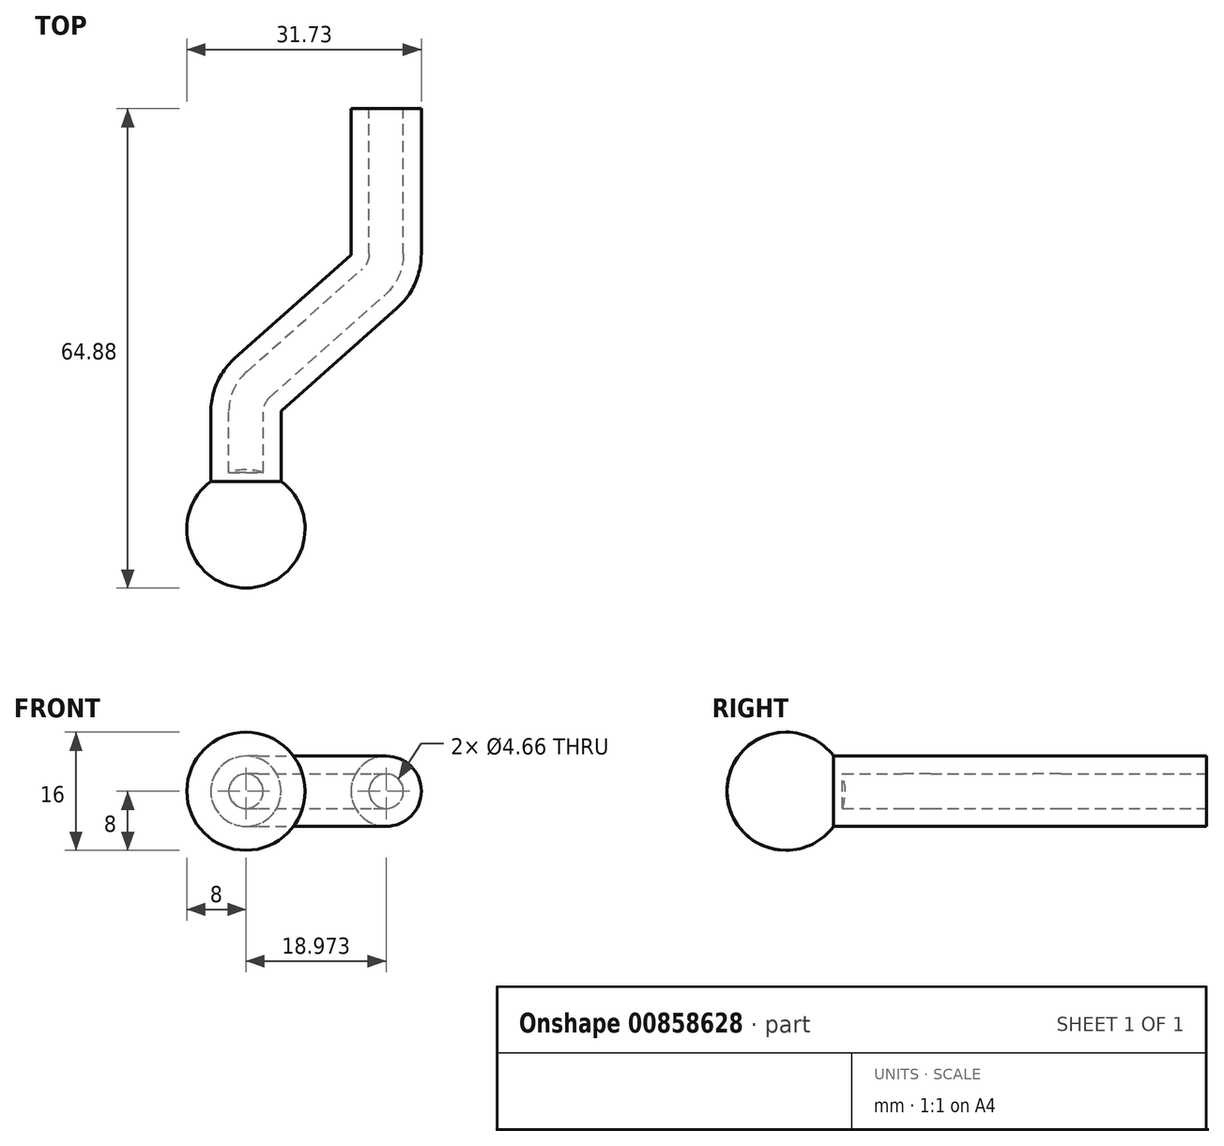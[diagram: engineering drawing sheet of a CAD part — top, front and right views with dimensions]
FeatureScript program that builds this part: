
annotation { "Feature Type Name" : "Feature", "Feature Type Description" : "" }
export const myFeature = defineFeature(function(context is Context, id is Id, definition is map)
    precondition{}
    {
        {
            var Q0;
            Q0=qCreatedBy(makeId("Top.planeOp"),FACE);
            var sketch = newSketch(context, id + "F0", { "sketchPlane" : qUnion([Q0])});
            skLineSegment(sketch, "E0", {"start": v(0, 0) * mm, "end": v(0, 11.78) * mm});
            skLineSegment(sketch, "E1", {"start": v(1.68, 15.51) * mm, "end": v(17.3, 29.4) * mm});
            skLineSegment(sketch, "E2", {"start": v(18.97, 33.14) * mm, "end": v(18.97, 52.83) * mm});
            skPoint(sketch, "E3.visualSharp", {"position": v(0, 14.02) * mm});
            skArc(sketch, "E3.filletArc", {"start": v(1.68, 15.51) * mm, "mid": v(0.44, 13.83) * mm, "end": v(0, 11.78) * mm});
            skPoint(sketch, "E4.visualSharp", {"position": v(18.97, 30.9) * mm});
            skArc(sketch, "E4.filletArc", {"start": v(17.3, 29.4) * mm, "mid": v(18.53, 31.1) * mm, "end": v(18.97, 33.14) * mm});
            skSolve(sketch);
        }
        {
            var Q0;
            Q0=qCreatedBy(makeId("Front.planeOp"),FACE);
            var sketch = newSketch(context, id + "F1", { "sketchPlane" : qUnion([Q0])});
            skCircle(sketch, "E5", {"center": v(0, 0) * mm, "radius": 4.76 * mm});
            skCircle(sketch, "E6", {"center": v(0, 0) * mm, "radius": 2.33 * mm});
            skSolve(sketch);
        }
        {
            var Q0;
            Q0=makeQuery(id+"F1.imprint","IMPRINT",FACE,{"disambiguationData":[TD([[makeQuery(id+"F1.imprint","IMPRINT",EDGE,{"derivedFrom":sQuery(id+"F1.wireOp",EDGE,"E5")}),1.0]])]});
            var Q1;
            Q1=sQuery(id+"F0.wireOp",EDGE,"E0");
            var Q2;
            Q2=sQuery(id+"F0.wireOp",EDGE,"E3.filletArc");
            var Q3;
            Q3=sQuery(id+"F0.wireOp",EDGE,"E1");
            var Q4;
            Q4=sQuery(id+"F0.wireOp",EDGE,"E4.filletArc");
            var Q5;
            Q5=sQuery(id+"F0.wireOp",EDGE,"E2");
            sweep(context, id + "F2", {"profiles" : qUnion([Q0]), "path" : qUnion([Q1, Q2, Q3, Q4, Q5])});
        }
        {
            var Q0;
            Q0=qCreatedBy(makeId("Right.planeOp"),FACE);
            var sketch = newSketch(context, id + "F3", { "sketchPlane" : qUnion([Q0])});
            skLineSegment(sketch, "E7", {"start": v(-4.05, 0) * mm, "end": v(-4.05, -8) * mm});
            skLineSegment(sketch, "E8", {"start": v(-4.05, 0) * mm, "end": v(-4.05, 8) * mm});
            skArc(sketch, "E9", {"start": v(-4.05, 8) * mm, "mid": v(-12.05, 0) * mm, "end": v(-4.05, -8) * mm});
            skPoint(sketch, "E9.third.point", {"position": v(-12.05, 0) * mm});
            skSolve(sketch);
        }
        {
            var Q0;
            Q0=makeQuery(id+"F3.imprint","IMPRINT",FACE,{"disambiguationData":[TD([[makeQuery(id+"F3.imprint","IMPRINT",EDGE,{"derivedFrom":sQuery(id+"F3.wireOp",EDGE,"E7")}),-1.0]])]});
            var Q1;
            Q1=sQuery(id+"F3.wireOp",EDGE,"E8");
            revolve(context, id + "F4", {"operationType" : NewBodyOperationType.ADD, "surfaceOperationType" : NewSurfaceOperationType.NEW, "entities" : qUnion([Q0]), "axis" : qUnion([Q1]), "revolveType" : RevolveType.FULL});
        }
    });
